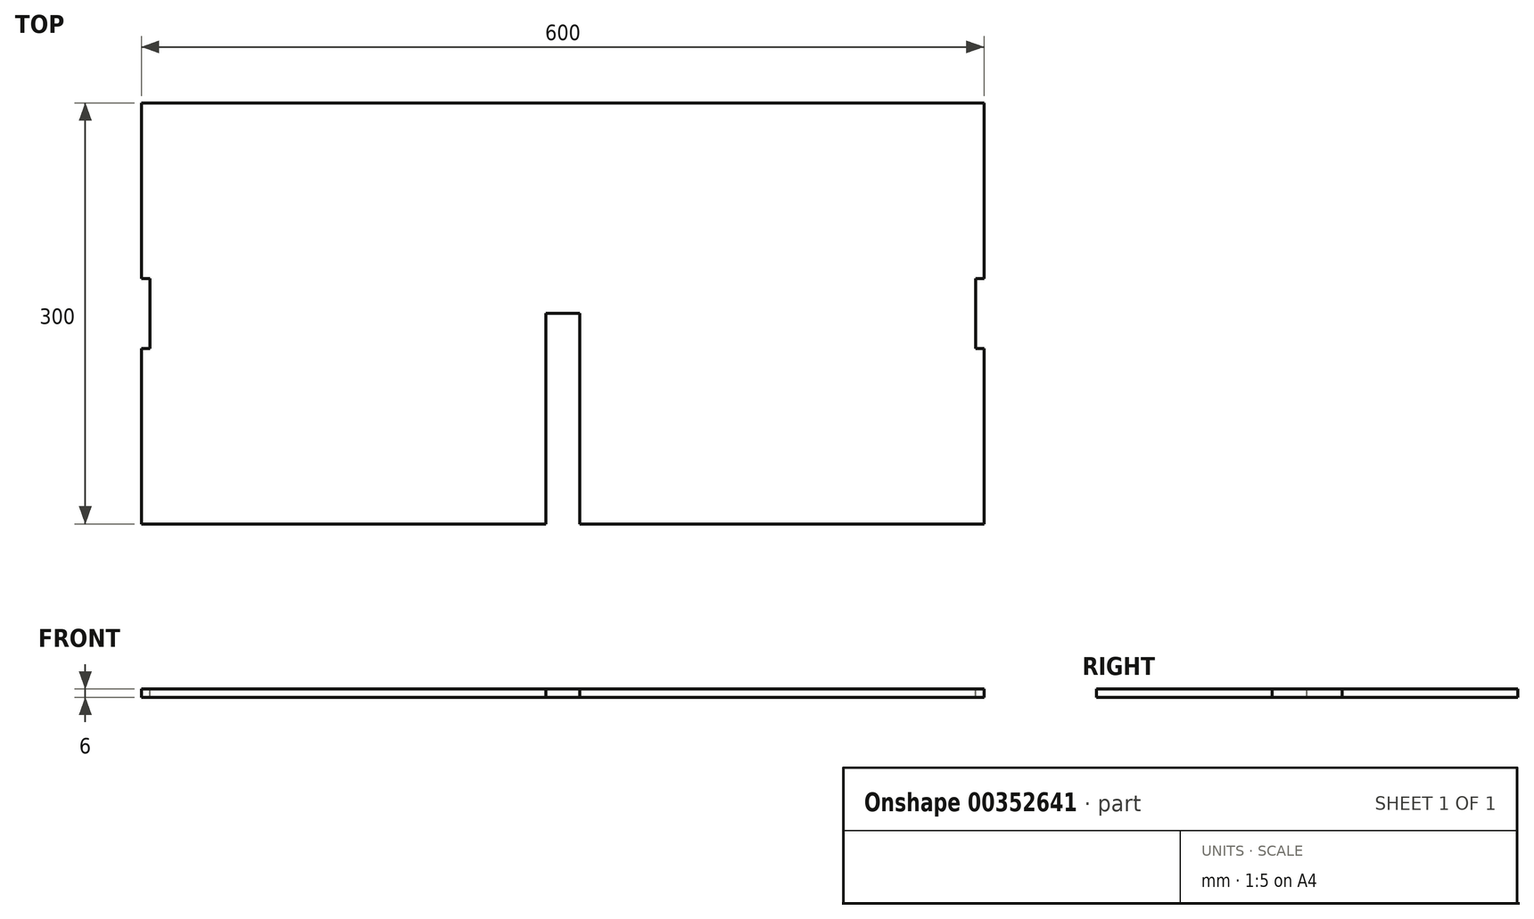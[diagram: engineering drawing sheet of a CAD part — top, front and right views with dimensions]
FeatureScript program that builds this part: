
annotation { "Feature Type Name" : "Feature", "Feature Type Description" : "" }
export const myFeature = defineFeature(function(context is Context, id is Id, definition is map)
    precondition{}
    {
        {
            var Q0;
            Q0=qCreatedBy(makeId("Front.planeOp"),FACE);
            var sketch = newSketch(context, id + "F0", { "sketchPlane" : qUnion([Q0])});
            skLineSegment(sketch, "E0.bottom", {"start": v(-213.98, 78.73) * mm, "end": v(386.02, 78.73) * mm});
            skLineSegment(sketch, "E0.top", {"start": v(-213.98, 72.73) * mm, "end": v(386.02, 72.73) * mm});
            skLineSegment(sketch, "E0.left", {"start": v(-213.98, 78.73) * mm, "end": v(-213.98, 72.73) * mm});
            skLineSegment(sketch, "E0.right", {"start": v(386.02, 78.73) * mm, "end": v(386.02, 72.73) * mm});
            skLineSegment(sketch, "E1", {"start": v(74.02, 78.73) * mm, "end": v(74.02, 72.73) * mm});
            skLineSegment(sketch, "E2", {"start": v(98.02, 78.73) * mm, "end": v(98.02, 72.73) * mm});
            skSolve(sketch);
        }
        {
            var Q0;
            Q0=qSketchRegion(id+"F0",true);
            extrude(context, id + "F1", {"entities" : qUnion([Q0]), "depth" : 300 * mm});
        }
        {
            var Q0;
            Q0=makeQuery(id+"F1.opExtrude","SWEPT_FACE",FACE,{"disambiguationData":[OSD([sQuery(id+"F0.wireOp",EDGE,"E0.bottom")])]});
            var sketch = newSketch(context, id + "F2", { "sketchPlane" : qUnion([Q0])});
            skLineSegment(sketch, "E3", {"start": v(-213.98, 0) * mm, "end": v(-213.98, -300) * mm});
            skLineSegment(sketch, "E4", {"start": v(386.02, 0) * mm, "end": v(386.02, -300) * mm});
            skLineSegment(sketch, "E5", {"start": v(98.02, -150) * mm, "end": v(98.02, -300) * mm});
            skLineSegment(sketch, "E6", {"start": v(74.02, -150) * mm, "end": v(74.02, -300) * mm});
            skLineSegment(sketch, "E7", {"start": v(98.02, -150) * mm, "end": v(74.02, -150) * mm});
            skLineSegment(sketch, "E8", {"start": v(-213.98, -175) * mm, "end": v(-207.98, -175) * mm});
            skLineSegment(sketch, "E9", {"start": v(-207.98, -175) * mm, "end": v(-207.98, -125) * mm});
            skLineSegment(sketch, "E10", {"start": v(-207.98, -125) * mm, "end": v(-213.98, -125) * mm});
            skLineSegment(sketch, "E11.MirrorCS", {"start": v(392.02, -175) * mm, "end": v(380.02, -175) * mm});
            skLineSegment(sketch, "E12.MirrorCS", {"start": v(380.02, -175) * mm, "end": v(380.02, -125) * mm});
            skLineSegment(sketch, "E13.MirrorCS", {"start": v(380.02, -125) * mm, "end": v(392.02, -125) * mm});
            skSolve(sketch);
        }
        {
            var Q0;
            {var subQ0=sQuery(id+"F2.wireOp",EDGE,"E8");Q0=makeQuery(id+"F2.imprint","IMPRINT",FACE,{"disambiguationData":[TD([[makeQuery(id+"F2.imprint","IMPRINT",EDGE,{"derivedFrom":subQ0}),1.0]])]});}
            var Q1;
            {var subQ0=sQuery(id+"F2.wireOp",EDGE,"E5");Q1=makeQuery(id+"F2.imprint","IMPRINT",FACE,{"disambiguationData":[TD([[makeQuery(id+"F2.imprint","IMPRINT",EDGE,{"derivedFrom":subQ0}),-1.0]])]});}
            var Q2;
            {var subQ0=sQuery(id+"F2.wireOp",EDGE,"E11.MirrorCS");Q2=makeQuery(id+"F2.imprint","IMPRINT",FACE,{"disambiguationData":[TD([[makeQuery(id+"F2.imprint","IMPRINT",EDGE,{"derivedFrom":subQ0}),-1.0]])]});}
            extrude(context, id + "F3", {"entities" : qUnion([Q0, Q1, Q2]), "operationType" : NewBodyOperationType.REMOVE, "oppositeDirection" : true, "depth" : 25 * mm});
        }
    });
